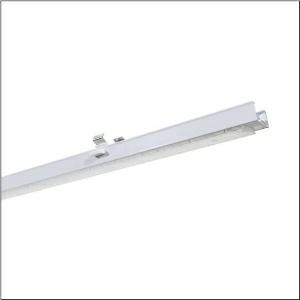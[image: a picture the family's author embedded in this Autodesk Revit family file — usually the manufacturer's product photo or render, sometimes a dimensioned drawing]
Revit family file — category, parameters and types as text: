
# Revit family: trunking_flex_31_51re14ma66b
name_source: partatom
category: Lighting Fixtures
units: mm (PartAtom-declared; Revit-internal decimal feet)

## family parameters
Cut with Voids When Loaded = No
Host = Face
Light Source = No
Part Type = Normal
Room Calculation Point = No
Round Connector Dimension = Use Diameter
Shared = No

## types (1)
- --- (1 x LED, 6400 lm, 40 W, 6500K)
    Apparent Load = 40 VA
    CIE Flux Codes = 72 92 98 99 100
    Color Rendering = 80
    Color Temperature = 6500K
    Default Elevation = 1800 mm
    Description = Trunking Flex 31, luminaire insert, of extruded aluminium section, coated, traffic white (RAL 9016), length: 1.172mm, width: 91mm, height: 53mm, LED rated luminous flux: 6.400lm, light colour: 865, SDCM (Standard Deviation of Colour Matching)MacAdam ≤ 3 SDCM (initial), control gear: ON/OFF Multilumen, with system connector: socket, mains connection: 220..240V, AC, 50/60Hz, rated input power: 40W, luminous flux adjustable on luminaire in four steps (3420/4540/5580/6630lm), connected load according to luminous flux setting (20/26/33/40W), primary light control with lens, of plastic, primary optical cover: cover, of PMMA, light emission: direct distribution, primary light characteristic: asymmetric, protection rating (complete): IP20, insulation class (complete): insulation class I (protective earthing), certification: CE, UKCA, impact resistance: IK02, permissible ambient temperature for indoor applications: -20..+40°C, packaging unit: 1 piece
    Height = 58 mm
    Lamp = 1 x LED
    Lamp Light Flux = 6400 lm
    Lamp Power = 40 W
    Lamp count = 1
    Length = 1172 mm
    Luminous efficacy = 160 lm/W
    Manufacturer = Siteco
    ModVariant = No
    Model = 51RE14MA66B
    Mounting Place = Ceiling
    Mounting Type = Pendant
    Number of Poles = 1
    OnlyDefault = Yes
    Power Factor = 1
    Product Name = Trunking Flex 31
    Product group = luminaire insert | ceiling pendant
    ProductGroupID = 901
    Protection Class = Protection class I
    Protection Degree = IP 20
    RLX_Detail_Level = 1
    RLX_Emergency_Light_Flux = 0 lm
    RLX_Emergency_Type = 0
    RLX_Emergency_Type_DB = No
    RlxData = <blob elided: 20837 chars, md5=56794650>
    Socket = socket
    Standby Power = 0 W
    System Light Flux = 6400 lm
    System Power = 40 W
    Type Comments = factory setting: luminous flux: 100 % | (ON | ON) | 300 mA
    Type Image = l_1266702.jpg
    URL = http://relux.com
    VarID = @adj_065629
    Voltage = 0 V
    Weight = 0.00 kg
    Width = 65 mm

## geometry (parser evidence)
native form markers: Blend x4, Sweep x13
no freeform markers — native parametric forms only
